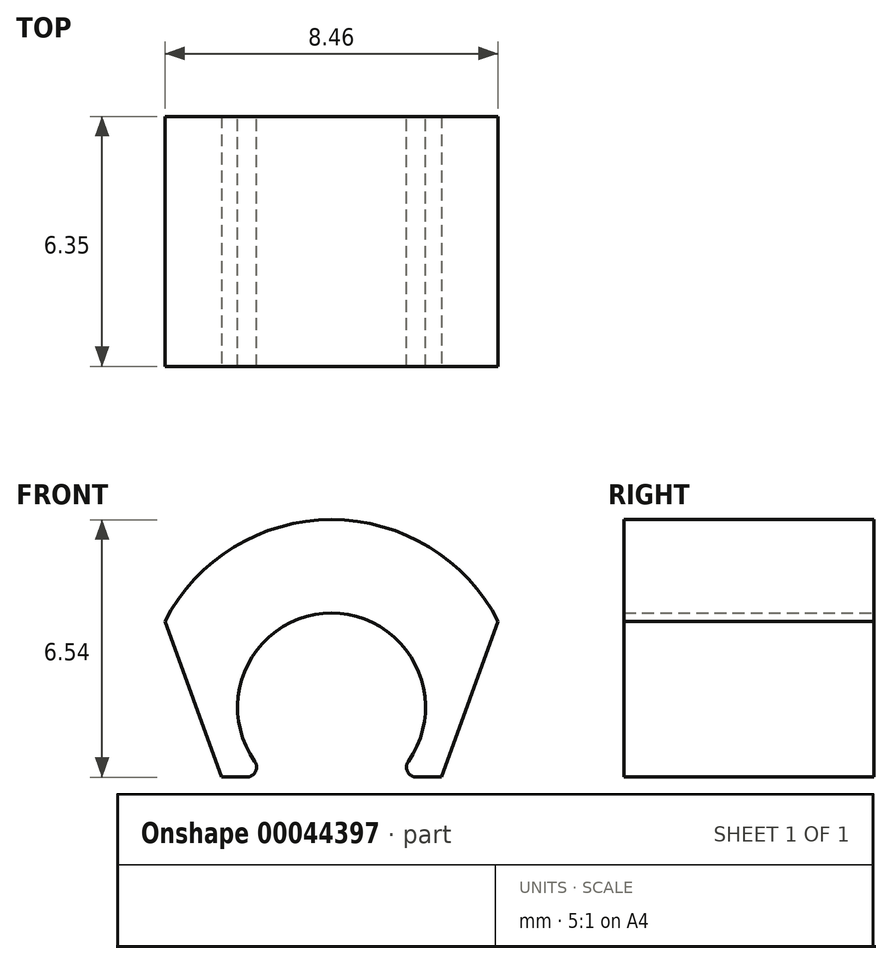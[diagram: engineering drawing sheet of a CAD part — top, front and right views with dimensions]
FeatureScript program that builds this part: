
annotation { "Feature Type Name" : "Feature", "Feature Type Description" : "" }
export const myFeature = defineFeature(function(context is Context, id is Id, definition is map)
    precondition{}
    {
        {
            var Q0;
            Q0=qCreatedBy(makeId("Front.planeOp"),FACE);
            var sketch = newSketch(context, id + "F0", { "sketchPlane" : qUnion([Q0])});
            skCircle(sketch, "E0", {"center": v(0, 0) * mm, "radius": 4.76 * mm});
            skCircle(sketch, "E1", {"center": v(0, 0) * mm, "radius": 2.39 * mm});
            skSolve(sketch);
        }
        {
            var Q0;
            Q0 = qSketchRegion(id + "F0", true);
            extrude(context, id + "F1", {"entities" : qUnion([Q0]), "depth" : 6.35 * mm});
        }
        {
            var Q0;
            Q0=makeQuery(id+"F1.opExtrude","CAP_FACE",FACE,{"disambiguationData":[OSD([sQuery(id+"F0.wireOp",EDGE,"E0"),sQuery(id+"F0.wireOp",EDGE,"E1")])],"isStart":false});
            var sketch = newSketch(context, id + "F2", { "sketchPlane" : qUnion([Q0])});
            skLineSegment(sketch, "E2", {"start": v(-4.86, 3.9) * mm, "end": v(-2.8, -1.78) * mm});
            skLineSegment(sketch, "E3", {"start": v(-2.8, -1.78) * mm, "end": v(2.8, -1.78) * mm});
            skLineSegment(sketch, "E4", {"start": v(2.8, -1.78) * mm, "end": v(5, 4.29) * mm});
            skLineSegment(sketch, "E5", {"start": v(5, 4.29) * mm, "end": v(6.37, 4.29) * mm});
            skLineSegment(sketch, "E6", {"start": v(6.37, 4.29) * mm, "end": v(6.37, -6.99) * mm});
            skLineSegment(sketch, "E7", {"start": v(6.37, -6.99) * mm, "end": v(-7.34, -6.99) * mm});
            skLineSegment(sketch, "E8", {"start": v(-7.34, -6.99) * mm, "end": v(-7.34, 3.9) * mm});
            skLineSegment(sketch, "E9", {"start": v(-7.34, 3.9) * mm, "end": v(-4.86, 3.9) * mm});
            skSolve(sketch);
        }
        {
            var Q0;
            Q0 = qSketchRegion(id + "F2", true);
            extrude(context, id + "F3", {"entities" : qUnion([Q0]), "operationType" : NewBodyOperationType.REMOVE, "endBound" : BoundingType.THROUGH_ALL, "oppositeDirection" : true, "depth" : 25.4 * mm});
        }
        {
            var Q0;
            Q0=makeQuery(id+"F3.boolean.opBoolean","INTERSECT",EDGE,{"disambiguationData":[OD(0.0)],"derivedFrom":[makeQuery(id+"F1.opExtrude","SWEPT_FACE",FACE,{"disambiguationData":[OSD([sQuery(id+"F0.wireOp",EDGE,"E1")])]}),makeQuery(id+"F3.opExtrude","SWEPT_FACE",FACE,{"disambiguationData":[OSD([sQuery(id+"F2.wireOp",EDGE,"E3")])]})]});
            var Q1;
            Q1=makeQuery(id+"F3.boolean.opBoolean","INTERSECT",EDGE,{"disambiguationData":[OD(1.0)],"derivedFrom":[makeQuery(id+"F1.opExtrude","SWEPT_FACE",FACE,{"disambiguationData":[OSD([sQuery(id+"F0.wireOp",EDGE,"E1")])]}),makeQuery(id+"F3.opExtrude","SWEPT_FACE",FACE,{"disambiguationData":[OSD([sQuery(id+"F2.wireOp",EDGE,"E3")])]})]});
            fillet(context, id + "F4", {"entities" : qUnion([Q0, Q1]), "radius" : 0.25 * mm, "tangentPropagation" : true, "allowEdgeOverflow" : false});
        }
    });
